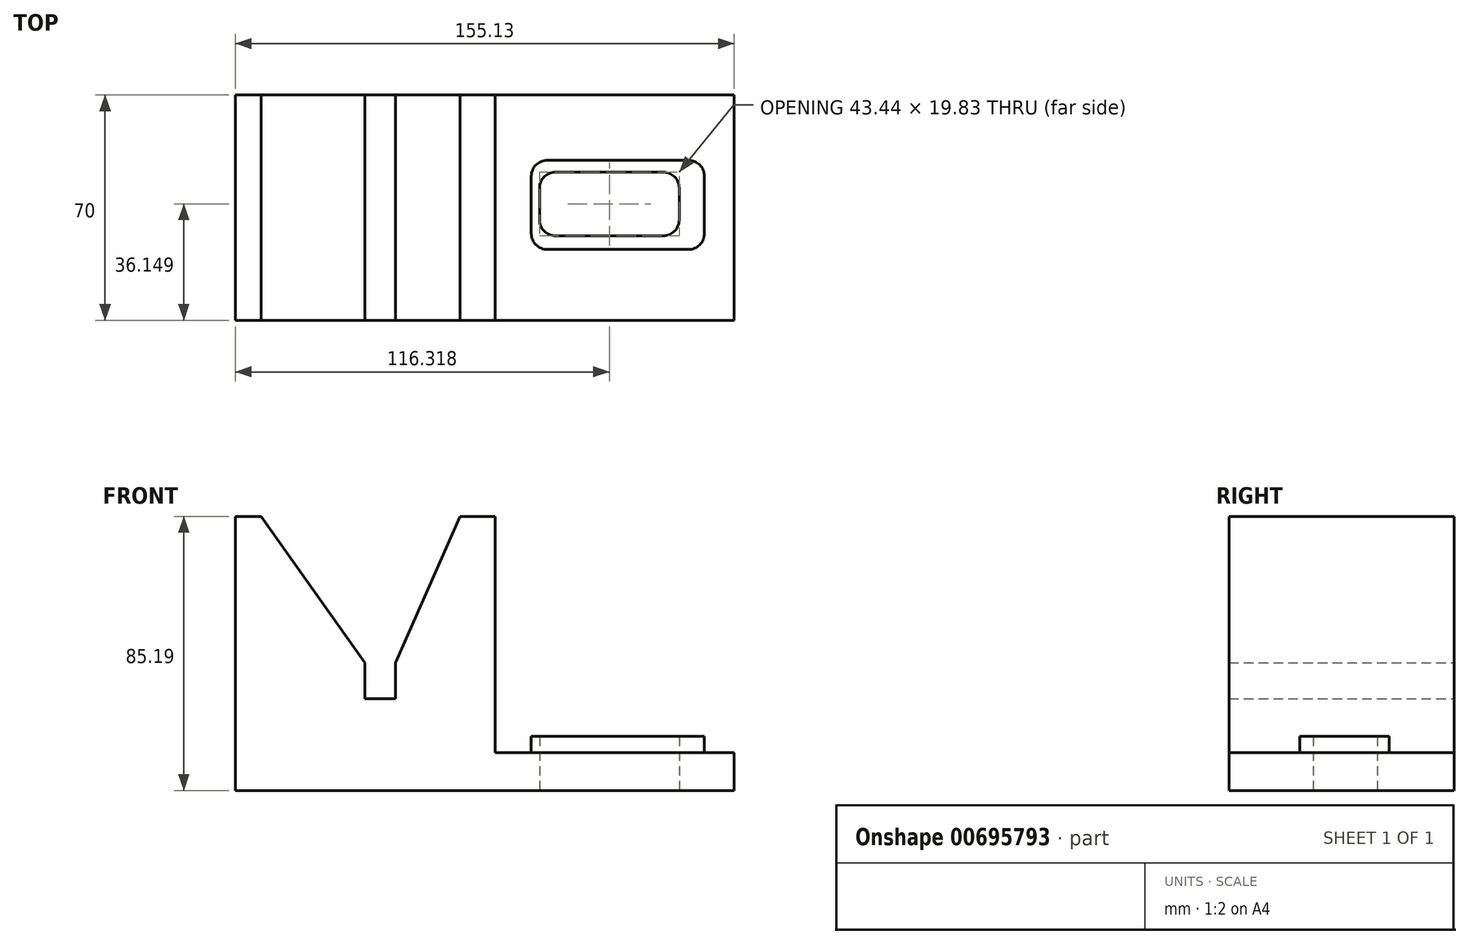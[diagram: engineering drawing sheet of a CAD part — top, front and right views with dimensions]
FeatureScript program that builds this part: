
annotation { "Feature Type Name" : "Feature", "Feature Type Description" : "" }
export const myFeature = defineFeature(function(context is Context, id is Id, definition is map)
    precondition{}
    {
        {
            var Q0;
            Q0=qCreatedBy(makeId("Front.planeOp"),FACE);
            var sketch = newSketch(context, id + "F0", { "sketchPlane" : qUnion([Q0])});
            skLineSegment(sketch, "E0", {"start": v(-62.89, 51.09) * mm, "end": v(-54.83, 51.09) * mm});
            skLineSegment(sketch, "E1", {"start": v(-62.89, 51.09) * mm, "end": v(-62.89, -34.1) * mm});
            skLineSegment(sketch, "E2", {"start": v(-62.89, -34.1) * mm, "end": v(92.24, -34.1) * mm});
            skLineSegment(sketch, "E3", {"start": v(92.24, -34.1) * mm, "end": v(92.24, -22.3) * mm});
            skLineSegment(sketch, "E4", {"start": v(92.24, -22.3) * mm, "end": v(17.99, -22.3) * mm});
            skLineSegment(sketch, "E5", {"start": v(17.99, -22.3) * mm, "end": v(17.99, 51.09) * mm});
            skLineSegment(sketch, "E6", {"start": v(17.99, 51.09) * mm, "end": v(7.05, 51.09) * mm});
            skLineSegment(sketch, "E7", {"start": v(7.05, 51.09) * mm, "end": v(-13.1, 5.61) * mm});
            skLineSegment(sketch, "E8", {"start": v(-13.1, 5.61) * mm, "end": v(-13.1, -5.61) * mm});
            skLineSegment(sketch, "E9", {"start": v(-13.1, -5.61) * mm, "end": v(-22.6, -5.61) * mm});
            skLineSegment(sketch, "E10", {"start": v(-22.6, -5.61) * mm, "end": v(-22.6, 5.61) * mm});
            skLineSegment(sketch, "E11", {"start": v(-22.6, 5.61) * mm, "end": v(-54.83, 51.09) * mm});
            skSolve(sketch);
        }
        {
            var Q0;
            Q0 = qSketchRegion(id + "F0", true);
            extrude(context, id + "F1", {"entities" : qUnion([Q0]), "depth" : 70 * mm, "offsetDistance" : 25 * mm});
        }
        {
            var Q0;
            Q0=makeQuery(id+"F1.opExtrude","SWEPT_FACE",FACE,{"disambiguationData":[OSD([sQuery(id+"F0.wireOp",EDGE,"E4")])]});
            var sketch = newSketch(context, id + "F2", { "sketchPlane" : qUnion([Q0])});
            skLineSegment(sketch, "E12.bottom", {"start": v(36.7, -23.94) * mm, "end": v(70.15, -23.94) * mm});
            skLineSegment(sketch, "E12.top", {"start": v(36.7, -43.77) * mm, "end": v(70.15, -43.77) * mm});
            skLineSegment(sketch, "E12.left", {"start": v(31.7, -28.94) * mm, "end": v(31.7, -38.77) * mm});
            skLineSegment(sketch, "E12.right", {"start": v(75.15, -28.94) * mm, "end": v(75.15, -38.77) * mm});
            skLineSegment(sketch, "E13.bottom", {"start": v(34.16, -20.25) * mm, "end": v(77.98, -20.25) * mm});
            skLineSegment(sketch, "E13.top", {"start": v(34.16, -48.01) * mm, "end": v(77.98, -48.01) * mm});
            skLineSegment(sketch, "E13.left", {"start": v(29.16, -25.25) * mm, "end": v(29.16, -43.01) * mm});
            skLineSegment(sketch, "E13.right", {"start": v(82.98, -25.25) * mm, "end": v(82.98, -43.01) * mm});
            skPoint(sketch, "E14.visualSharp", {"position": v(31.7, -23.94) * mm});
            skArc(sketch, "E14.filletArc", {"start": v(36.7, -23.94) * mm, "mid": v(33.17, -25.4) * mm, "end": v(31.7, -28.94) * mm});
            skPoint(sketch, "E15.visualSharp", {"position": v(75.15, -23.94) * mm});
            skArc(sketch, "E15.filletArc", {"start": v(75.15, -28.94) * mm, "mid": v(73.68, -25.4) * mm, "end": v(70.15, -23.94) * mm});
            skPoint(sketch, "E16.visualSharp", {"position": v(75.15, -43.77) * mm});
            skArc(sketch, "E16.filletArc", {"start": v(70.15, -43.77) * mm, "mid": v(73.68, -42.3) * mm, "end": v(75.15, -38.77) * mm});
            skPoint(sketch, "E17.visualSharp", {"position": v(31.7, -43.77) * mm});
            skArc(sketch, "E17.filletArc", {"start": v(31.7, -38.77) * mm, "mid": v(33.17, -42.3) * mm, "end": v(36.7, -43.77) * mm});
            skPoint(sketch, "E18.visualSharp", {"position": v(29.16, -20.25) * mm});
            skArc(sketch, "E18.filletArc", {"start": v(34.16, -20.25) * mm, "mid": v(30.62, -21.72) * mm, "end": v(29.16, -25.25) * mm});
            skPoint(sketch, "E19.visualSharp", {"position": v(82.98, -20.25) * mm});
            skArc(sketch, "E19.filletArc", {"start": v(82.98, -25.25) * mm, "mid": v(81.52, -21.72) * mm, "end": v(77.98, -20.25) * mm});
            skPoint(sketch, "E20.visualSharp", {"position": v(82.98, -48.01) * mm});
            skArc(sketch, "E20.filletArc", {"start": v(77.98, -48.01) * mm, "mid": v(81.52, -46.55) * mm, "end": v(82.98, -43.01) * mm});
            skPoint(sketch, "E21.visualSharp", {"position": v(29.16, -48.01) * mm});
            skArc(sketch, "E21.filletArc", {"start": v(29.16, -43.01) * mm, "mid": v(30.62, -46.55) * mm, "end": v(34.16, -48.01) * mm});
            skSolve(sketch);
        }
        {
            var Q0;
            Q0 = qSketchRegion(id + "F2", true);
            extrude(context, id + "F3", {"entities" : qUnion([Q0]), "operationType" : NewBodyOperationType.ADD, "depth" : 5 * mm, "offsetDistance" : 25 * mm});
        }
        {
            var Q0;
            Q0=makeQuery(id+"F3.boolean.opBoolean","SPLIT",FACE,{"disambiguationData":[TD([makeQuery(id+"F3.opExtrude","SWEPT_FACE",FACE,{"disambiguationData":[OSD([sQuery(id+"F2.wireOp",EDGE,"E12.bottom")])]})])],"derivedFrom":makeQuery(id+"F1.opExtrude","SWEPT_FACE",FACE,{"disambiguationData":[OSD([sQuery(id+"F0.wireOp",EDGE,"E4")])]})});
            extrude(context, id + "F4", {"entities" : qUnion([Q0]), "operationType" : NewBodyOperationType.REMOVE, "oppositeDirection" : true, "depth" : 25 * mm, "offsetDistance" : 25 * mm});
        }
    });
